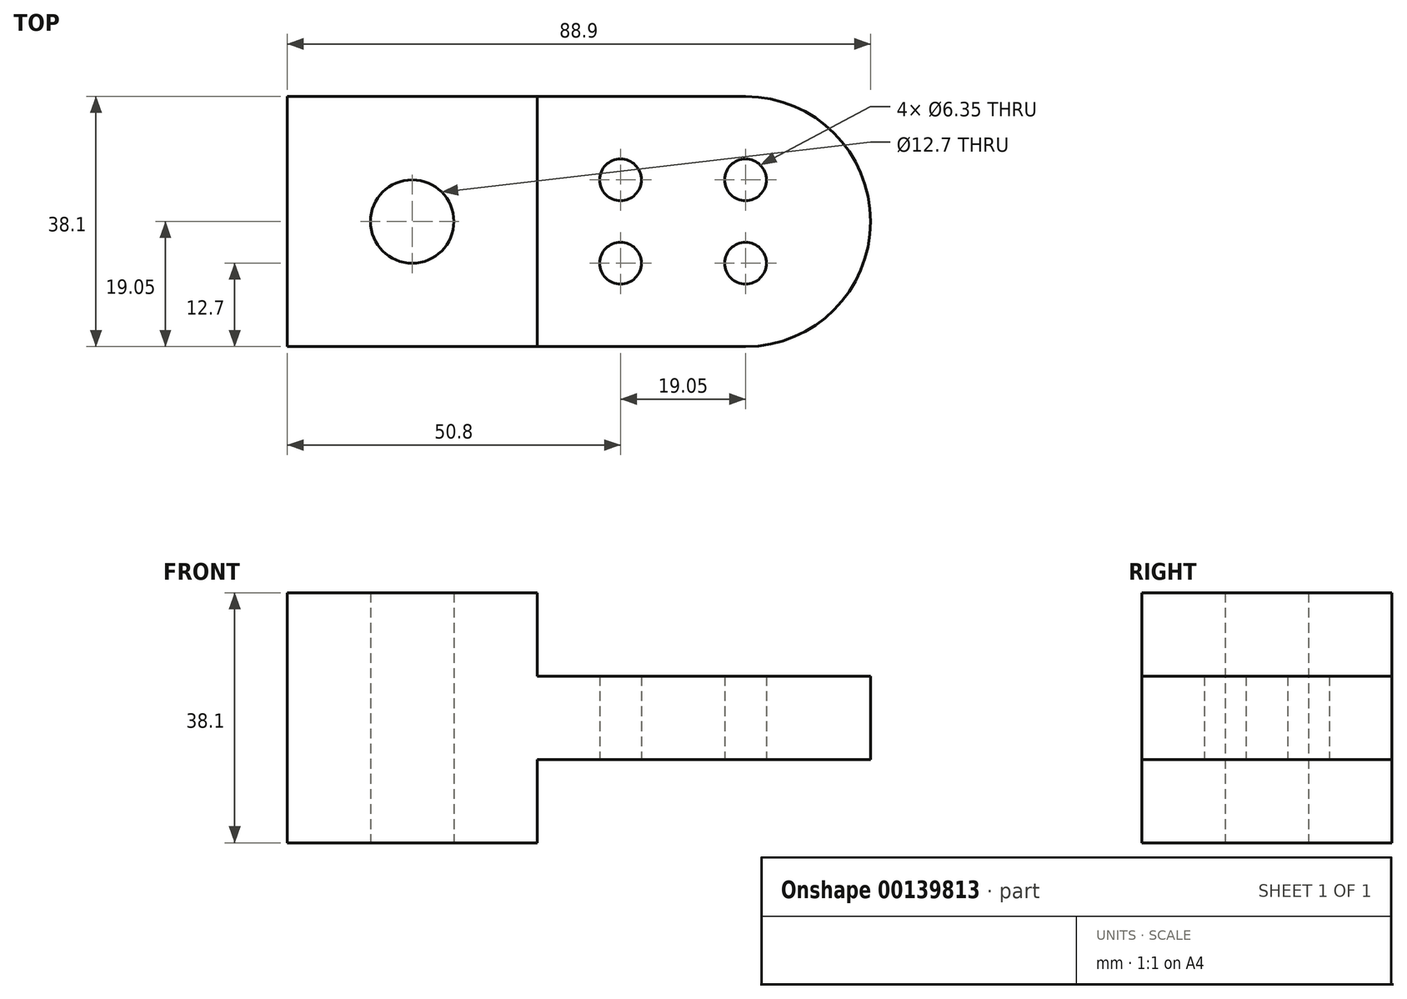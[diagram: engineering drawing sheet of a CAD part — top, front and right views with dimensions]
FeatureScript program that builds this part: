
annotation { "Feature Type Name" : "Feature", "Feature Type Description" : "" }
export const myFeature = defineFeature(function(context is Context, id is Id, definition is map)
    precondition{}
    {
        {
            var Q0;
            Q0=qCreatedBy(makeId("Top.planeOp"),FACE);
            var sketch = newSketch(context, id + "F0", { "sketchPlane" : qUnion([Q0])});
            skLineSegment(sketch, "E0.bottom", {"start": v(19.05, -19.05) * mm, "end": v(-19.05, -19.05) * mm});
            skLineSegment(sketch, "E0.top", {"start": v(19.05, 19.05) * mm, "end": v(-19.05, 19.05) * mm});
            skLineSegment(sketch, "E0.left", {"start": v(19.05, -19.05) * mm, "end": v(19.05, 19.05) * mm});
            skLineSegment(sketch, "E0.right", {"start": v(-19.05, -19.05) * mm, "end": v(-19.05, 19.05) * mm});
            skPoint(sketch, "E0.middle", {"position": v(0, 0) * mm});
            skCircle(sketch, "E1", {"center": v(0, 0) * mm, "radius": 6.35 * mm});
            skLineSegment(sketch, "E2", {"start": v(19.05, 19.05) * mm, "end": v(50.8, 19.05) * mm});
            skLineSegment(sketch, "E3", {"start": v(19.05, -19.05) * mm, "end": v(50.8, -19.05) * mm});
            skArc(sketch, "E4", {"start": v(50.8, -19.05) * mm, "mid": v(69.85, 0) * mm, "end": v(50.8, 19.05) * mm});
            skCircle(sketch, "E5", {"center": v(31.75, 6.35) * mm, "radius": 3.18 * mm});
            skCircle(sketch, "E6", {"center": v(31.75, -6.35) * mm, "radius": 3.18 * mm});
            skCircle(sketch, "E7", {"center": v(50.8, 6.35) * mm, "radius": 3.18 * mm});
            skCircle(sketch, "E8", {"center": v(50.8, -6.35) * mm, "radius": 3.18 * mm});
            skSolve(sketch);
        }
        {
            var Q0;
            Q0=makeQuery(id+"F0.imprint","IMPRINT",FACE,{"disambiguationData":[TD([[makeQuery(id+"F0.imprint","IMPRINT",EDGE,{"derivedFrom":sQuery(id+"F0.wireOp",EDGE,"E0.bottom")}),-1.0]])]});
            extrude(context, id + "F1", {"entities" : qUnion([Q0]), "depth" : 38.1 * mm});
        }
        {
            var Q0;
            Q0=makeQuery(id+"F0.imprint","IMPRINT",FACE,{"disambiguationData":[TD([[makeQuery(id+"F0.imprint","IMPRINT",EDGE,{"derivedFrom":sQuery(id+"F0.wireOp",EDGE,"E0.left")}),-1.0]])]});
            extrude(context, id + "F2", {"entities" : qUnion([Q0]), "operationType" : NewBodyOperationType.ADD, "depth" : 25.4 * mm, "hasSecondDirection" : true, "secondDirectionOppositeDirection" : false, "secondDirectionDepth" : 12.7 * mm});
        }
    });
